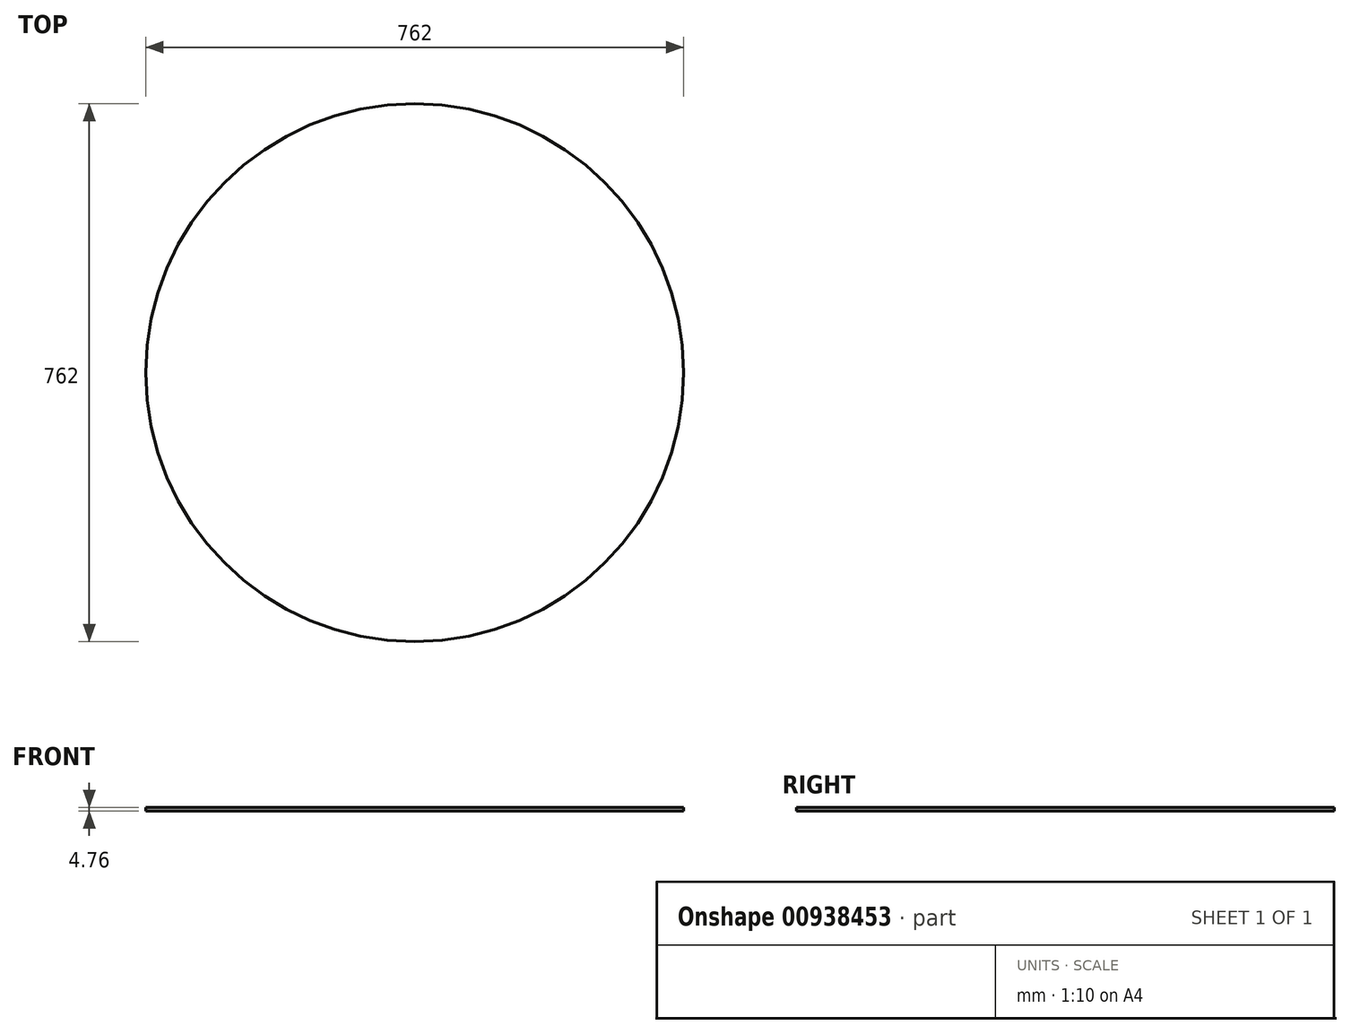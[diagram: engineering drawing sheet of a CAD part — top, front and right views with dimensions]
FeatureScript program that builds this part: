
annotation { "Feature Type Name" : "Feature", "Feature Type Description" : "" }
export const myFeature = defineFeature(function(context is Context, id is Id, definition is map)
    precondition{}
    {
        {
            var Q0;
            Q0=qCreatedBy(makeId("Top.planeOp"),FACE);
            var sketch = newSketch(context, id + "F0", { "sketchPlane" : qUnion([Q0])});
            skCircle(sketch, "E0", {"center": v(0, 0) * mm, "radius": 381 * mm});
            skLineSegment(sketch, "E1", {"start": v(-325.92, -30.33) * mm, "end": v(-266.8, -80.45) * mm});
            skSolve(sketch);
        }
        {
            var Q0;
            Q0=makeQuery(id+"F0.imprint","IMPRINT",FACE,{"disambiguationData":[TD([[makeQuery(id+"F0.imprint","IMPRINT",EDGE,{"derivedFrom":sQuery(id+"F0.wireOp",EDGE,"E0")}),1.0]])]});
            extrude(context, id + "F1", {"entities" : qUnion([Q0]), "depth" : 4.76 * mm, "offsetDistance" : 25.4 * mm});
        }
    });
